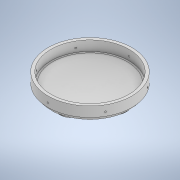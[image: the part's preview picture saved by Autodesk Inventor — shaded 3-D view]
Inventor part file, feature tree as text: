
AUTODESK INVENTOR PART (.ipt)
format: ipt  version: 2022 (Build 260153000, 153)  size: 213,504 bytes
history: native  units: mm
features: sketch x5, revolve x3, pattern_circular x2, extrude x2
ambient origin geometry x8: Origin, YZ Plane, XZ Plane, XY Plane, X Axis, Y Axis, Z Axis, Center Point
bodies: Body1 (feature_tree)
feature tree (12):
  revolve  "Revolution1"  [1 undecoded]
  revolve  "Revolution2"  [1 undecoded]
  revolve  "Revolution4"  Angle=360.0deg
  pattern_circular  "Circular Pattern2"  Count=4 Angle=360.0deg
  extrude  "Extrusion3"  Depth=0.75mm
  extrude  "Extrusion4"  Depth=2.0mm
  pattern_circular  "Circular Pattern3"  [2 undecoded]
  sketch  "Sketch2"  dims[d3=50.0mm d4=48.0mm]
  sketch  "Sketch3"  dims[d5=90.0deg d6=10.0mm]
  sketch  "Sketch4"  dims[d7=51.75mm d8=360.0deg]
  sketch  "Sketch6"  dims[d18=13.962634mm d19=40.0mm d20=360.0deg]
  sketch  "Sketch7"  dims[d22=5.0mm d23=0.0mm d24=0.75mm d26=2.0mm d27=0.0mm d28=0.0mm d29=60.0mm d30=360.0deg]
note: 4 required parameter values undecoded (feature->parameter linkage not recoverable at this tier; creation-order binding heuristic only, values carry confidence <= 0.55)